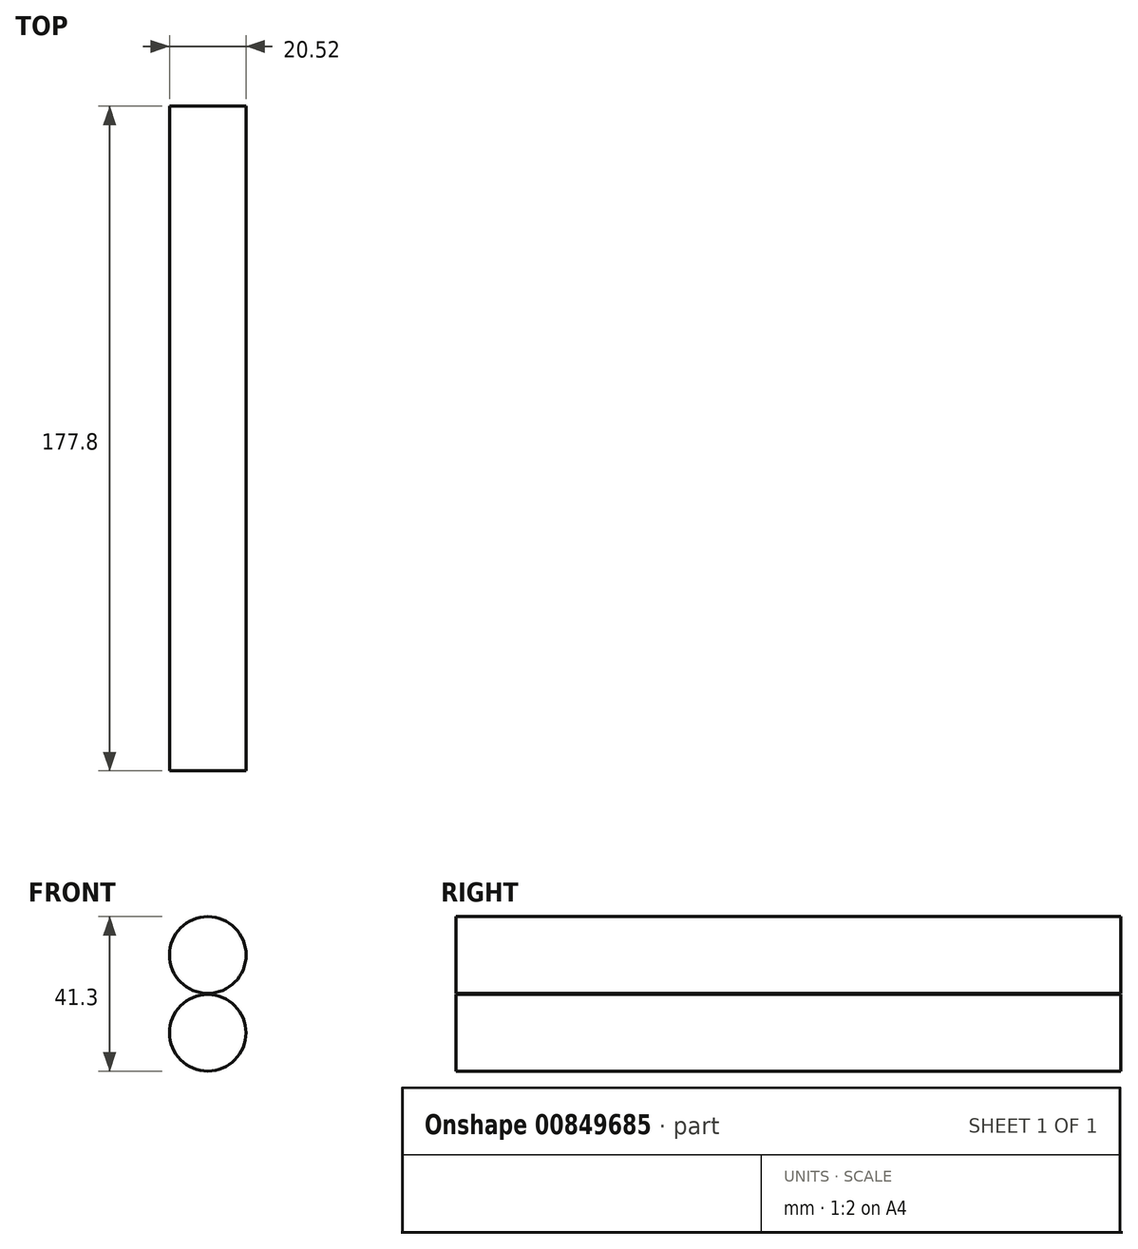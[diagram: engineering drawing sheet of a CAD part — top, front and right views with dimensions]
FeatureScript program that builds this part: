
annotation { "Feature Type Name" : "Feature", "Feature Type Description" : "" }
export const myFeature = defineFeature(function(context is Context, id is Id, definition is map)
    precondition{}
    {
        {
            var Q0;
            Q0=qCreatedBy(makeId("Front.planeOp"),FACE);
            var sketch = newSketch(context, id + "F0", { "sketchPlane" : qUnion([Q0])});
            skCircle(sketch, "E0", {"center": v(0, 0) * mm, "radius": 10.26 * mm});
            skCircle(sketch, "E1", {"center": v(0, -20.8) * mm, "radius": 10.23 * mm});
            skSolve(sketch);
        }
        {
            var Q0;
            Q0=makeQuery(id+"F0.imprint","IMPRINT",FACE,{"disambiguationData":[TD([[makeQuery(id+"F0.imprint","IMPRINT",EDGE,{"derivedFrom":sQuery(id+"F0.wireOp",EDGE,"E0")}),1.0]])]});
            var Q1;
            Q1=makeQuery(id+"F0.imprint","IMPRINT",FACE,{"disambiguationData":[TD([[makeQuery(id+"F0.imprint","IMPRINT",EDGE,{"derivedFrom":sQuery(id+"F0.wireOp",EDGE,"E1")}),1.0]])]});
            extrude(context, id + "F1", {"entities" : qUnion([Q0, Q1]), "depth" : 177.8 * mm, "offsetDistance" : 25.4 * mm});
        }
    });
